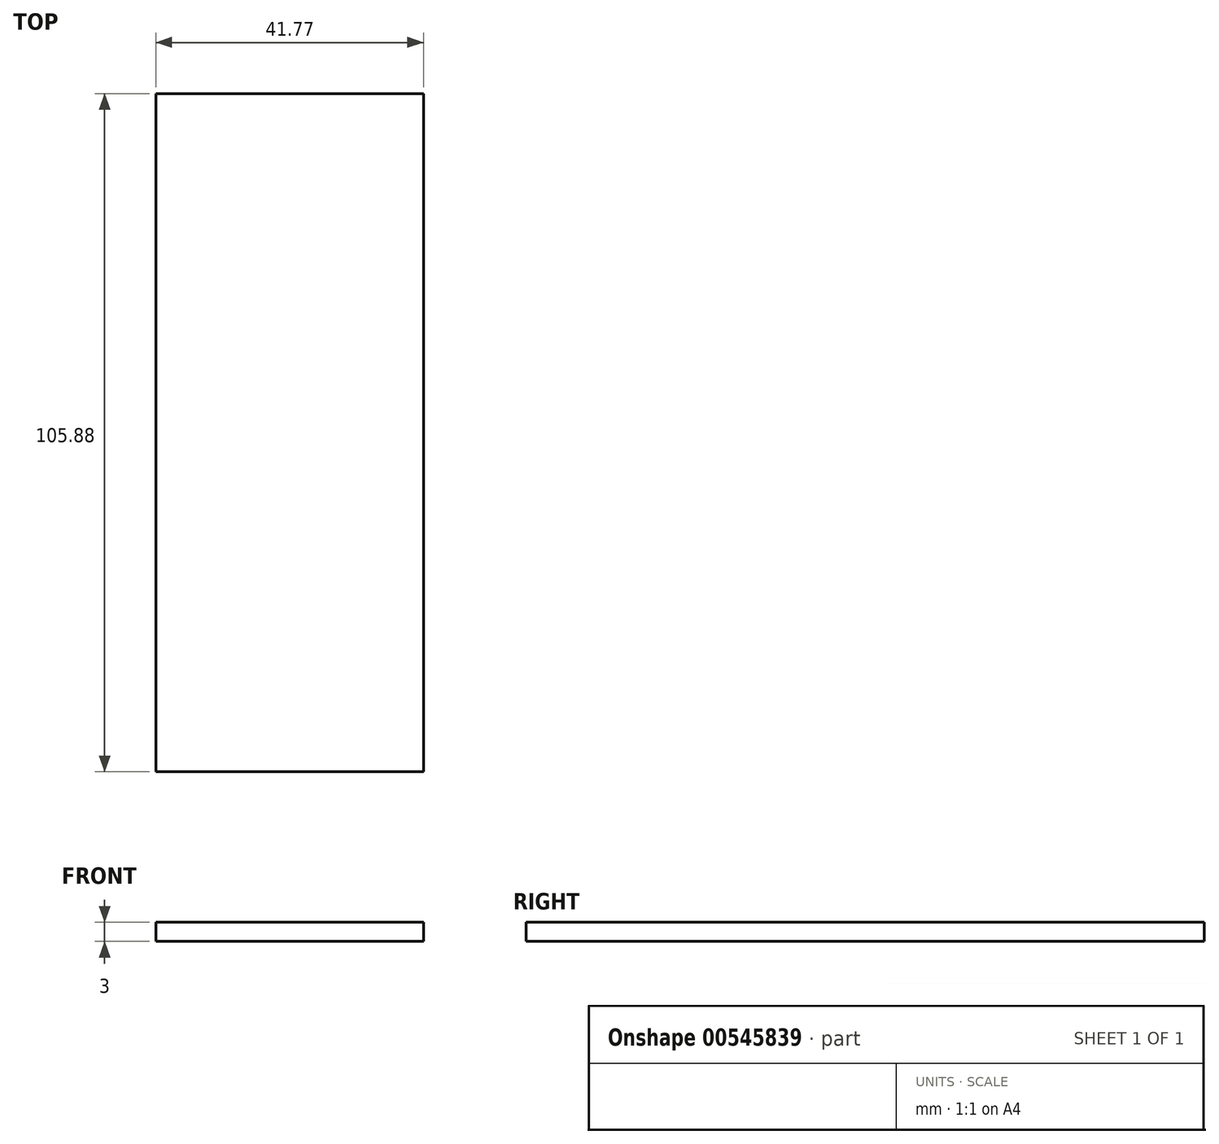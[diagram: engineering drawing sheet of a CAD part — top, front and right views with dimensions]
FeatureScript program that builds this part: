
annotation { "Feature Type Name" : "Feature", "Feature Type Description" : "" }
export const myFeature = defineFeature(function(context is Context, id is Id, definition is map)
    precondition{}
    {
        {
            var Q0;
            Q0=qCreatedBy(makeId("Top.planeOp"),FACE);
            var sketch = newSketch(context, id + "F0", { "sketchPlane" : qUnion([Q0])});
            skLineSegment(sketch, "E0.bottom", {"start": v(0, 0) * mm, "end": v(41.77, 0) * mm});
            skLineSegment(sketch, "E0.top", {"start": v(0, 105.88) * mm, "end": v(41.77, 105.88) * mm});
            skLineSegment(sketch, "E0.left", {"start": v(0, 0) * mm, "end": v(0, 105.88) * mm});
            skLineSegment(sketch, "E0.right", {"start": v(41.77, 0) * mm, "end": v(41.77, 105.88) * mm});
            skSolve(sketch);
        }
        {
            var Q0;
            Q0 = qSketchRegion(id + "F0", true);
            extrude(context, id + "F1", {"entities" : qUnion([Q0]), "depth" : 3 * mm, "offsetDistance" : 25.4 * mm});
        }
    });
